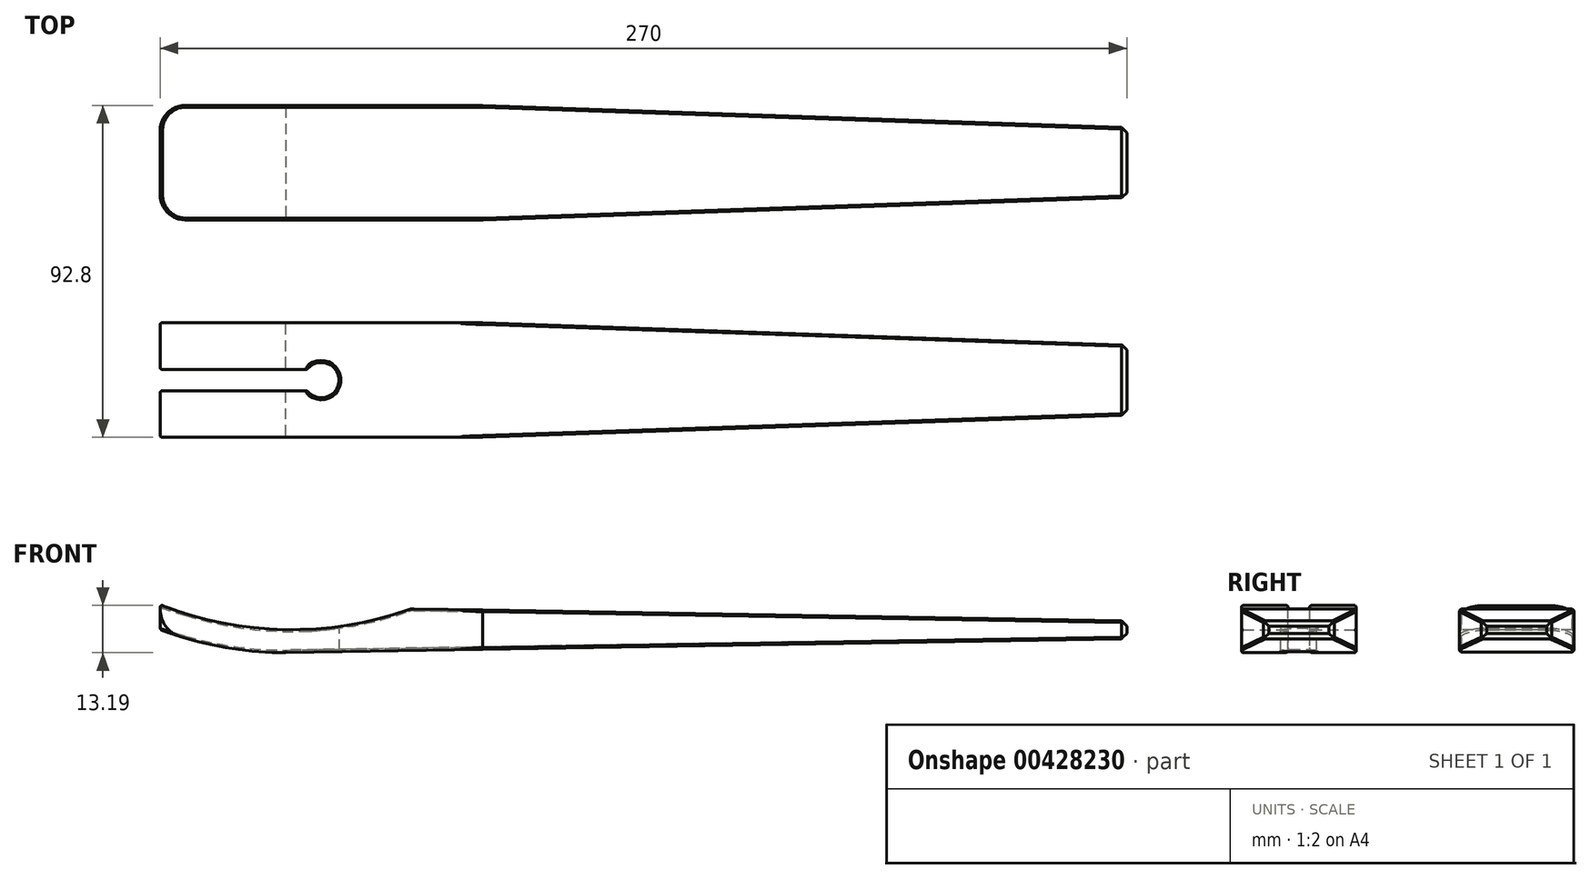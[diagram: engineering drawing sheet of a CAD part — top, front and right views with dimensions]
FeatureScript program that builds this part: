
annotation { "Feature Type Name" : "Feature", "Feature Type Description" : "" }
export const myFeature = defineFeature(function(context is Context, id is Id, definition is map)
    precondition{}
    {
        {
            var Q0;
            Q0=qCreatedBy(makeId("Front.planeOp"),FACE);
            var sketch = newSketch(context, id + "F0", { "sketchPlane" : qUnion([Q0])});
            skLineSegment(sketch, "E0", {"start": v(0, 0) * mm, "end": v(-270, 0) * mm, "construction": true});
            skLineSegment(sketch, "E1", {"start": v(-270, 0) * mm, "end": v(-270, 7) * mm, "construction": true});
            skLineSegment(sketch, "E2", {"start": v(0, 0) * mm, "end": v(0, 2.5) * mm, "construction": true});
            skLineSegment(sketch, "E3", {"start": v(0, 0) * mm, "end": v(0, -2.5) * mm, "construction": true});
            skLineSegment(sketch, "E4", {"start": v(-270, 7) * mm, "end": v(-270, 0) * mm});
            skLineSegment(sketch, "E5", {"start": v(-235, -6.42) * mm, "end": v(0, -2.5) * mm});
            skLineSegment(sketch, "E6", {"start": v(0, 2.5) * mm, "end": v(-200, 5.83) * mm});
            skLineSegment(sketch, "E7", {"start": v(-200, -5.83) * mm, "end": v(-200, 5.83) * mm, "construction": true});
            skLineSegment(sketch, "E8", {"start": v(-270, 0) * mm, "end": v(-235, 0) * mm, "construction": true});
            skLineSegment(sketch, "E9", {"start": v(-235, 0) * mm, "end": v(-200, 0) * mm, "construction": true});
            skArc(sketch, "E10", {"start": v(-270, 7) * mm, "mid": v(-235.1, 0) * mm, "end": v(-200, 5.83) * mm});
            skLineSegment(sketch, "E11", {"start": v(-235, 0) * mm, "end": v(-235, -6.42) * mm, "construction": true});
            skArc(sketch, "E12", {"start": v(-270, 0) * mm, "mid": v(-252.8, -4.8) * mm, "end": v(-235, -6.42) * mm});
            skLineSegment(sketch, "E13", {"start": v(0, -2.5) * mm, "end": v(0, 2.5) * mm});
            skSolve(sketch);
        }
        {
            var Q0;
            Q0=makeQuery(id+"F0.imprint","IMPRINT",FACE,{"disambiguationData":[TD([[makeQuery(id+"F0.imprint","IMPRINT",EDGE,{"derivedFrom":sQuery(id+"F0.wireOp",EDGE,"E4")}),1.0]])]});
            extrude(context, id + "F1", {"entities" : qUnion([Q0]), "depth" : 32 * mm});
        }
        {
            var Q0;
            Q0=qCreatedBy(makeId("Top.planeOp"),FACE);
            var sketch = newSketch(context, id + "F2", { "sketchPlane" : qUnion([Q0])});
            skLineSegment(sketch, "E14", {"start": v(0, 0) * mm, "end": v(0, -16) * mm, "construction": true});
            skLineSegment(sketch, "E15", {"start": v(0, -16) * mm, "end": v(-270, -16) * mm, "construction": true});
            skLineSegment(sketch, "E16", {"start": v(-270, -16) * mm, "end": v(-270, -19) * mm, "construction": true});
            skLineSegment(sketch, "E17", {"start": v(-270, -16) * mm, "end": v(-270, -13) * mm});
            skLineSegment(sketch, "E18", {"start": v(-270, -16) * mm, "end": v(-225, -16) * mm, "construction": true});
            skCircle(sketch, "E19", {"center": v(-225, -16) * mm, "radius": 5 * mm});
            skLineSegment(sketch, "E20", {"start": v(-270, -13) * mm, "end": v(-229, -13) * mm});
            skLineSegment(sketch, "E21", {"start": v(-229, -13) * mm, "end": v(-229, -19) * mm});
            skLineSegment(sketch, "E22", {"start": v(-229, -19) * mm, "end": v(-270, -19) * mm});
            skLineSegment(sketch, "E23", {"start": v(-270, -19) * mm, "end": v(-270, -13) * mm});
            skSolve(sketch);
        }
        {
            var Q0;
            Q0 = qSketchRegion(id + "F2", true);
            extrude(context, id + "F3", {"entities" : qUnion([Q0]), "operationType" : NewBodyOperationType.REMOVE, "endBound" : BoundingType.SYMMETRIC, "oppositeDirection" : true, "depth" : 25 * mm});
        }
        {
            var Q0;
            {var subQ0=sQuery(id+"F0.wireOp",EDGE,"E4");var subQ1=sQuery(id+"F0.wireOp",EDGE,"E12");Q0=makeQuery(id+"F3.boolean.opBoolean","SPLIT",EDGE,{"disambiguationData":[TD([makeQuery(id+"F3.opExtrude","SWEPT_FACE",FACE,{"disambiguationData":[OSD([sQuery(id+"F2.wireOp",EDGE,"E20")])]})])],"derivedFrom":makeQuery(id+"F1.opExtrude","SWEPT_EDGE",EDGE,{"disambiguationData":[OSD([subQ0,subQ1])]})});}
            var Q1;
            {var subQ0=sQuery(id+"F0.wireOp",EDGE,"E4");var subQ1=sQuery(id+"F0.wireOp",EDGE,"E12");Q1=makeQuery(id+"F3.boolean.opBoolean","SPLIT",EDGE,{"disambiguationData":[TD([makeQuery(id+"F3.opExtrude","SWEPT_FACE",FACE,{"disambiguationData":[OSD([sQuery(id+"F2.wireOp",EDGE,"E22")])]})])],"derivedFrom":makeQuery(id+"F1.opExtrude","SWEPT_EDGE",EDGE,{"disambiguationData":[OSD([subQ0,subQ1])]})});}
            fillet(context, id + "F4", {"entities" : qUnion([Q0, Q1]), "radius" : 8 * mm, "tangentPropagation" : true, "allowEdgeOverflow" : false});
        }
        {
            var Q0;
            {var subQ0=sQuery(id+"F0.wireOp",EDGE,"E4");var subQ1=sQuery(id+"F0.wireOp",EDGE,"E10");Q0=makeQuery(id+"F3.boolean.opBoolean","SPLIT",EDGE,{"disambiguationData":[TD([makeQuery(id+"F3.opExtrude","SWEPT_FACE",FACE,{"disambiguationData":[OSD([sQuery(id+"F2.wireOp",EDGE,"E20")])]})])],"derivedFrom":makeQuery(id+"F1.opExtrude","SWEPT_EDGE",EDGE,{"disambiguationData":[OSD([subQ0,subQ1])]})});}
            var Q1;
            {var subQ0=sQuery(id+"F0.wireOp",EDGE,"E4");var subQ1=sQuery(id+"F0.wireOp",EDGE,"E10");Q1=makeQuery(id+"F3.boolean.opBoolean","SPLIT",EDGE,{"disambiguationData":[TD([makeQuery(id+"F3.opExtrude","SWEPT_FACE",FACE,{"disambiguationData":[OSD([sQuery(id+"F2.wireOp",EDGE,"E22")])]})])],"derivedFrom":makeQuery(id+"F1.opExtrude","SWEPT_EDGE",EDGE,{"disambiguationData":[OSD([subQ0,subQ1])]})});}
            fillet(context, id + "F5", {"entities" : qUnion([Q0, Q1]), "radius" : 0.5 * mm, "tangentPropagation" : true, "allowEdgeOverflow" : false});
        }
        {
            var Q0;
            Q0=makeQuery(id+"F1.opExtrude","SWEPT_EDGE",EDGE,{"disambiguationData":[OSD([sQuery(id+"F0.wireOp",EDGE,"E6"),sQuery(id+"F0.wireOp",EDGE,"E10")])]});
            fillet(context, id + "F6", {"entities" : qUnion([Q0]), "radius" : 5 * mm, "tangentPropagation" : true, "allowEdgeOverflow" : false});
        }
        {
            var Q0;
            Q0=qCreatedBy(makeId("Top.planeOp"),FACE);
            var sketch = newSketch(context, id + "F7", { "sketchPlane" : qUnion([Q0])});
            skLineSegment(sketch, "E24", {"start": v(0, -16) * mm, "end": v(0, -21) * mm, "construction": true});
            skLineSegment(sketch, "E25", {"start": v(0, -16) * mm, "end": v(0, -11) * mm, "construction": true});
            skLineSegment(sketch, "E26", {"start": v(-180, 0) * mm, "end": v(-180, -32) * mm, "construction": true});
            skLineSegment(sketch, "E27", {"start": v(0, -16) * mm, "end": v(0, -10) * mm, "construction": true});
            skLineSegment(sketch, "E28", {"start": v(0, -16) * mm, "end": v(-8.82, -16) * mm, "construction": true});
            skLineSegment(sketch, "E29.MirrorCS", {"start": v(0, -22) * mm, "end": v(0, -32) * mm});
            skLineSegment(sketch, "E30", {"start": v(0, 0) * mm, "end": v(-180, 0) * mm});
            skLineSegment(sketch, "E31", {"start": v(0, 0) * mm, "end": v(-5, 0) * mm, "construction": true});
            skLineSegment(sketch, "E32", {"start": v(-5, 0) * mm, "end": v(-5, -11) * mm, "construction": true});
            skLineSegment(sketch, "E33", {"start": v(0, 0) * mm, "end": v(0, -6) * mm, "construction": true});
            skLineSegment(sketch, "E34", {"start": v(0, -6) * mm, "end": v(-5, -6) * mm, "construction": true});
            skLineSegment(sketch, "E35", {"start": v(-5, -6) * mm, "end": v(-5, -11) * mm, "construction": true});
            skLineSegment(sketch, "E36", {"start": v(-180, 0) * mm, "end": v(-5, -6) * mm});
            skLineSegment(sketch, "E37", {"start": v(0, -11) * mm, "end": v(0, 0) * mm});
            skLineSegment(sketch, "E38.MirrorCS", {"start": v(0, -21) * mm, "end": v(0, -32) * mm});
            skLineSegment(sketch, "E39.MirrorCS", {"start": v(0, -32) * mm, "end": v(-180, -32) * mm});
            skLineSegment(sketch, "E40.MirrorCS", {"start": v(-180, -32) * mm, "end": v(-5, -26) * mm});
            skLineSegment(sketch, "E41", {"start": v(-5, -26) * mm, "end": v(0, -25.83) * mm});
            skLineSegment(sketch, "E42.trimOffspring", {"start": v(0, -25.83) * mm, "end": v(0, -32) * mm, "construction": true});
            skLineSegment(sketch, "E43", {"start": v(-5, -6) * mm, "end": v(0, -6.17) * mm});
            skSolve(sketch);
        }
        {
            var Q0;
            Q0 = qSketchRegion(id + "F7", true);
            extrude(context, id + "F8", {"entities" : qUnion([Q0]), "operationType" : NewBodyOperationType.REMOVE, "endBound" : BoundingType.SYMMETRIC, "depth" : 25 * mm});
        }
        {
            var Q0;
            Q0=makeQuery(id+"F1.opExtrude","SWEPT_FACE",FACE,{"disambiguationData":[OSD([sQuery(id+"F0.wireOp",EDGE,"E13")])]});
            chamfer(context, id + "F9", {"entities" : qUnion([Q0]), "width" : 1.5 * mm, "tangentPropagation" : true});
        }
        {
            var Q0;
            Q0=makeQuery(id+"F8.boolean.opBoolean","INTERSECT",EDGE,{"derivedFrom":[makeQuery(id+"F1.opExtrude","SWEPT_FACE",FACE,{"disambiguationData":[OSD([sQuery(id+"F0.wireOp",EDGE,"E6")])]}),makeQuery(id+"F8.opExtrude","SWEPT_FACE",FACE,{"disambiguationData":[OSD([sQuery(id+"F7.wireOp",EDGE,"E36"),sQuery(id+"F7.wireOp",EDGE,"E43")])]})]});
            var Q1;
            Q1=makeQuery(id+"F8.boolean.opBoolean","INTERSECT",EDGE,{"derivedFrom":[makeQuery(id+"F1.opExtrude","SWEPT_FACE",FACE,{"disambiguationData":[OSD([sQuery(id+"F0.wireOp",EDGE,"E6")])]}),makeQuery(id+"F8.opExtrude","SWEPT_FACE",FACE,{"disambiguationData":[OSD([sQuery(id+"F7.wireOp",EDGE,"E40.MirrorCS"),sQuery(id+"F7.wireOp",EDGE,"E41")])]})]});
            var Q2;
            Q2=makeQuery(id+"F8.boolean.opBoolean","INTERSECT",EDGE,{"derivedFrom":[makeQuery(id+"F1.opExtrude","SWEPT_FACE",FACE,{"disambiguationData":[OSD([sQuery(id+"F0.wireOp",EDGE,"E5")])]}),makeQuery(id+"F8.opExtrude","SWEPT_FACE",FACE,{"disambiguationData":[OSD([sQuery(id+"F7.wireOp",EDGE,"E36"),sQuery(id+"F7.wireOp",EDGE,"E43")])]})]});
            var Q3;
            Q3=makeQuery(id+"F8.boolean.opBoolean","INTERSECT",EDGE,{"derivedFrom":[makeQuery(id+"F1.opExtrude","SWEPT_FACE",FACE,{"disambiguationData":[OSD([sQuery(id+"F0.wireOp",EDGE,"E5")])]}),makeQuery(id+"F8.opExtrude","SWEPT_FACE",FACE,{"disambiguationData":[OSD([sQuery(id+"F7.wireOp",EDGE,"E40.MirrorCS"),sQuery(id+"F7.wireOp",EDGE,"E41")])]})]});
            chamfer(context, id + "F10", {"entities" : qUnion([Q0, Q1, Q2, Q3]), "width" : .5 * mm, "tangentPropagation" : true});
        }
        {
            var Q0;
            Q0=makeQuery(id+"F1.opExtrude","CAP_EDGE",EDGE,{"disambiguationData":[OSD([sQuery(id+"F0.wireOp",EDGE,"E10")])],"isStart":true});
            var Q1;
            Q1=makeQuery(id+"F3.boolean.opBoolean","INTERSECT",EDGE,{"derivedFrom":[makeQuery(id+"F1.opExtrude","SWEPT_FACE",FACE,{"disambiguationData":[OSD([sQuery(id+"F0.wireOp",EDGE,"E10")])]}),makeQuery(id+"F3.opExtrude","SWEPT_FACE",FACE,{"disambiguationData":[OSD([sQuery(id+"F2.wireOp",EDGE,"E20")])]})]});
            var Q2;
            Q2=makeQuery(id+"F3.boolean.opBoolean","INTERSECT",EDGE,{"derivedFrom":[makeQuery(id+"F1.opExtrude","SWEPT_FACE",FACE,{"disambiguationData":[OSD([sQuery(id+"F0.wireOp",EDGE,"E10")])]}),makeQuery(id+"F3.opExtrude","SWEPT_FACE",FACE,{"disambiguationData":[OSD([sQuery(id+"F2.wireOp",EDGE,"E22")])]})]});
            var Q3;
            Q3=makeQuery(id+"F3.boolean.opBoolean","INTERSECT",EDGE,{"derivedFrom":[makeQuery(id+"F1.opExtrude","SWEPT_FACE",FACE,{"disambiguationData":[OSD([sQuery(id+"F0.wireOp",EDGE,"E10")])]}),makeQuery(id+"F3.opExtrude","SWEPT_FACE",FACE,{"disambiguationData":[OSD([sQuery(id+"F2.wireOp",EDGE,"E19")])]})]});
            var Q4;
            Q4=makeQuery(id+"F1.opExtrude","CAP_EDGE",EDGE,{"disambiguationData":[OSD([sQuery(id+"F0.wireOp",EDGE,"E10")])],"isStart":false});
            fillet(context, id + "F11", {"entities" : qUnion([Q0, Q1, Q2, Q3, Q4]), "radius" : .5 * mm, "tangentPropagation" : true, "allowEdgeOverflow" : false});
        }
        {
            var Q0;
            Q0=makeQuery(id+"F3.boolean.opBoolean","INTERSECT",EDGE,{"derivedFrom":[makeQuery(id+"F1.opExtrude","SWEPT_FACE",FACE,{"disambiguationData":[OSD([sQuery(id+"F0.wireOp",EDGE,"E5")])]}),makeQuery(id+"F3.opExtrude","SWEPT_FACE",FACE,{"disambiguationData":[OSD([sQuery(id+"F2.wireOp",EDGE,"E19")])]})]});
            fillet(context, id + "F12", {"entities" : qUnion([Q0]), "radius" : .5 * mm, "tangentPropagation" : true, "allowEdgeOverflow" : false});
        }
        {
            var Q0;
            Q0=qCreatedBy(makeId("Front.planeOp"),FACE);
            cPlane(context, id + "F13", {"entities" : qUnion([Q0]), "cplaneType" : CPlaneType.OFFSET, "offset" : 28.8 * mm, "oppositeDirection" : true, "width" : 150 * mm, "height" : 150 * mm});
        }
        {
            var Q0;
            Q0=qCreatedBy(id+"F13.planeOp",FACE);
            var sketch = newSketch(context, id + "F14", { "sketchPlane" : qUnion([Q0])});
            skLineSegment(sketch, "E44", {"start": v(0, 0) * mm, "end": v(-270, 0) * mm, "construction": true});
            skLineSegment(sketch, "E45", {"start": v(-270, 0) * mm, "end": v(-270, 7) * mm, "construction": true});
            skLineSegment(sketch, "E46", {"start": v(0, 0) * mm, "end": v(0, 2.5) * mm, "construction": true});
            skLineSegment(sketch, "E47", {"start": v(0, 0) * mm, "end": v(0, -2.5) * mm, "construction": true});
            skLineSegment(sketch, "E48", {"start": v(-270, 7) * mm, "end": v(-270, 0) * mm});
            skLineSegment(sketch, "E49", {"start": v(-235, -6.2) * mm, "end": v(0, -2.5) * mm});
            skLineSegment(sketch, "E50", {"start": v(0, 2.5) * mm, "end": v(-200, 5.83) * mm});
            skLineSegment(sketch, "E51", {"start": v(-200, -5.65) * mm, "end": v(-200, 5.83) * mm, "construction": true});
            skLineSegment(sketch, "E52", {"start": v(-270, 0) * mm, "end": v(-235, 0) * mm, "construction": true});
            skLineSegment(sketch, "E53", {"start": v(-235, 0) * mm, "end": v(-200, 0.09) * mm, "construction": true});
            skArc(sketch, "E54", {"start": v(-270, 7) * mm, "mid": v(-235.1, 0) * mm, "end": v(-200, 5.83) * mm});
            skLineSegment(sketch, "E55", {"start": v(-235, 0) * mm, "end": v(-235, -6.2) * mm, "construction": true});
            skArc(sketch, "E56", {"start": v(-270, 0) * mm, "mid": v(-252.77, -4.65) * mm, "end": v(-235, -6.2) * mm});
            skLineSegment(sketch, "E57", {"start": v(0, -2.5) * mm, "end": v(0, 2.5) * mm});
            skSolve(sketch);
        }
        {
            var Q0;
            Q0 = qSketchRegion(id + "F14", true);
            extrude(context, id + "F15", {"entities" : qUnion([Q0]), "oppositeDirection" : true, "depth" : 32 * mm});
        }
        {
            var Q0;
            Q0=qCreatedBy(makeId("Top.planeOp"),FACE);
            var sketch = newSketch(context, id + "F16", { "sketchPlane" : qUnion([Q0])});
            skLineSegment(sketch, "E58", {"start": v(0, 28.8) * mm, "end": v(0, 49.8) * mm, "construction": true});
            skLineSegment(sketch, "E59", {"start": v(0, 60.8) * mm, "end": v(-180, 60.8) * mm});
            skLineSegment(sketch, "E60", {"start": v(0, 54.62) * mm, "end": v(0, 44.8) * mm, "construction": true});
            skLineSegment(sketch, "E61", {"start": v(0, 44.8) * mm, "end": v(0, 49.8) * mm, "construction": true});
            skLineSegment(sketch, "E62", {"start": v(0, 49.8) * mm, "end": v(-5, 49.8) * mm, "construction": true});
            skLineSegment(sketch, "E63", {"start": v(-5, 49.8) * mm, "end": v(-5, 54.8) * mm, "construction": true});
            skLineSegment(sketch, "E64", {"start": v(-5, 54.8) * mm, "end": v(-180, 60.8) * mm});
            skLineSegment(sketch, "E65", {"start": v(-5, 54.8) * mm, "end": v(0, 54.62) * mm});
            skLineSegment(sketch, "E66", {"start": v(0, 44.8) * mm, "end": v(-13.59, 44.8) * mm, "construction": true});
            skLineSegment(sketch, "E67", {"start": v(0, 54.62) * mm, "end": v(0, 60.8) * mm});
            skLineSegment(sketch, "E68.MirrorCS", {"start": v(-5, 34.8) * mm, "end": v(0, 34.96) * mm});
            skLineSegment(sketch, "E69.MirrorCS", {"start": v(-5, 34.8) * mm, "end": v(-180, 28.8) * mm});
            skLineSegment(sketch, "E70.MirrorCS", {"start": v(0, 28.8) * mm, "end": v(-180, 28.8) * mm});
            skLineSegment(sketch, "E71.MirrorCS", {"start": v(0, 34.96) * mm, "end": v(0, 28.8) * mm});
            skSolve(sketch);
        }
        {
            var Q0;
            Q0 = qSketchRegion(id + "F16", true);
            extrude(context, id + "F17", {"entities" : qUnion([Q0]), "operationType" : NewBodyOperationType.REMOVE, "endBound" : BoundingType.SYMMETRIC, "oppositeDirection" : true, "depth" : 25 * mm});
        }
        {
            var Q0;
            Q0=makeQuery(id+"F15.opExtrude","SWEPT_EDGE",EDGE,{"disambiguationData":[OSD([sQuery(id+"F14.wireOp",EDGE,"E50"),sQuery(id+"F14.wireOp",EDGE,"E54")])]});
            fillet(context, id + "F18", {"entities" : qUnion([Q0]), "radius" : 5 * mm, "tangentPropagation" : true, "allowEdgeOverflow" : false});
        }
        {
            var Q0;
            Q0=makeQuery(id+"F15.opExtrude","CAP_EDGE",EDGE,{"disambiguationData":[OSD([sQuery(id+"F14.wireOp",EDGE,"E48")])],"isStart":true});
            var Q1;
            Q1=makeQuery(id+"F15.opExtrude","CAP_EDGE",EDGE,{"disambiguationData":[OSD([sQuery(id+"F14.wireOp",EDGE,"E48")])],"isStart":false});
            fillet(context, id + "F19", {"entities" : qUnion([Q0, Q1]), "radius" : 7 * mm, "tangentPropagation" : true, "allowEdgeOverflow" : false});
        }
        {
            var Q0;
            Q0=makeQuery(id+"F15.opExtrude","SWEPT_FACE",FACE,{"disambiguationData":[OSD([sQuery(id+"F14.wireOp",EDGE,"E57")])]});
            chamfer(context, id + "F20", {"entities" : qUnion([Q0]), "width" : 1.5 * mm, "tangentPropagation" : true});
        }
        {
            var Q0;
            Q0=makeQuery(id+"F17.boolean.opBoolean","INTERSECT",EDGE,{"derivedFrom":[makeQuery(id+"F15.opExtrude","SWEPT_FACE",FACE,{"disambiguationData":[OSD([sQuery(id+"F14.wireOp",EDGE,"E50")])]}),makeQuery(id+"F17.opExtrude","SWEPT_FACE",FACE,{"disambiguationData":[OSD([sQuery(id+"F16.wireOp",EDGE,"E68.MirrorCS"),sQuery(id+"F16.wireOp",EDGE,"E69.MirrorCS")])]})]});
            var Q1;
            Q1=makeQuery(id+"F17.boolean.opBoolean","INTERSECT",EDGE,{"derivedFrom":[makeQuery(id+"F15.opExtrude","SWEPT_FACE",FACE,{"disambiguationData":[OSD([sQuery(id+"F14.wireOp",EDGE,"E50")])]}),makeQuery(id+"F17.opExtrude","SWEPT_FACE",FACE,{"disambiguationData":[OSD([sQuery(id+"F16.wireOp",EDGE,"E64"),sQuery(id+"F16.wireOp",EDGE,"E65")])]})]});
            var Q2;
            Q2=makeQuery(id+"F17.boolean.opBoolean","INTERSECT",EDGE,{"derivedFrom":[makeQuery(id+"F15.opExtrude","SWEPT_FACE",FACE,{"disambiguationData":[OSD([sQuery(id+"F14.wireOp",EDGE,"E49")])]}),makeQuery(id+"F17.opExtrude","SWEPT_FACE",FACE,{"disambiguationData":[OSD([sQuery(id+"F16.wireOp",EDGE,"E64"),sQuery(id+"F16.wireOp",EDGE,"E65")])]})]});
            var Q3;
            Q3=makeQuery(id+"F15.opExtrude","CAP_EDGE",EDGE,{"disambiguationData":[OSD([sQuery(id+"F14.wireOp",EDGE,"E50")])],"isStart":false});
            var Q4;
            Q4=makeQuery(id+"F15.opExtrude","CAP_EDGE",EDGE,{"disambiguationData":[OSD([sQuery(id+"F14.wireOp",EDGE,"E54")])],"isStart":false});
            var Q5;
            Q5=makeQuery(id+"F15.opExtrude","CAP_EDGE",EDGE,{"disambiguationData":[OSD([sQuery(id+"F14.wireOp",EDGE,"E49")])],"isStart":false});
            var Q6;
            Q6=makeQuery(id+"F15.opExtrude","CAP_EDGE",EDGE,{"disambiguationData":[OSD([sQuery(id+"F14.wireOp",EDGE,"E56")])],"isStart":false});
            var Q7;
            Q7=makeQuery(id+"F17.boolean.opBoolean","INTERSECT",EDGE,{"derivedFrom":[makeQuery(id+"F15.opExtrude","SWEPT_FACE",FACE,{"disambiguationData":[OSD([sQuery(id+"F14.wireOp",EDGE,"E49")])]}),makeQuery(id+"F17.opExtrude","SWEPT_FACE",FACE,{"disambiguationData":[OSD([sQuery(id+"F16.wireOp",EDGE,"E68.MirrorCS"),sQuery(id+"F16.wireOp",EDGE,"E69.MirrorCS")])]})]});
            var Q8;
            {var subQ0=sQuery(id+"F14.wireOp",EDGE,"E56");var subQ1=sQuery(id+"F14.wireOp",EDGE,"E49");Q8=makeQuery(id+"F17.boolean.opBoolean","SPLIT",EDGE,{"disambiguationData":[TD([makeQuery(id+"F15.opExtrude","SWEPT_FACE",FACE,{"disambiguationData":[OSD([subQ0])]})])],"derivedFrom":makeQuery(id+"F15.opExtrude","CAP_EDGE",EDGE,{"disambiguationData":[OSD([subQ1])],"isStart":true})});}
            var Q9;
            Q9=makeQuery(id+"F15.opExtrude","CAP_EDGE",EDGE,{"disambiguationData":[OSD([sQuery(id+"F14.wireOp",EDGE,"E56")])],"isStart":true});
            var Q10;
            Q10=makeQuery(id+"F15.opExtrude","CAP_EDGE",EDGE,{"disambiguationData":[OSD([sQuery(id+"F14.wireOp",EDGE,"E54")])],"isStart":true});
            var Q11;
            {var subQ0=sQuery(id+"F14.wireOp",EDGE,"E54");var subQ1=sQuery(id+"F14.wireOp",EDGE,"E50");Q11=makeQuery(id+"F17.boolean.opBoolean","SPLIT",EDGE,{"disambiguationData":[TD([makeQuery(id+"F15.opExtrude","SWEPT_FACE",FACE,{"disambiguationData":[OSD([subQ0])]})])],"derivedFrom":makeQuery(id+"F15.opExtrude","CAP_EDGE",EDGE,{"disambiguationData":[OSD([subQ1])],"isStart":true})});}
            chamfer(context, id + "F21", {"entities" : qUnion([Q0, Q1, Q2, Q3, Q4, Q5, Q6, Q7, Q8, Q9, Q10, Q11]), "width" : 0.5 * mm, "tangentPropagation" : true});
        }
    });
